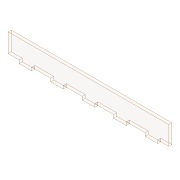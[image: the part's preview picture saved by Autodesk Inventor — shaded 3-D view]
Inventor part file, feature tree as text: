
AUTODESK INVENTOR PART (.ipt)
format: ipt  version: 2020 (Build 240168000, 168)  size: 113,152 bytes
history: native  units: in
note: dims shown in document units (in); Inventor stores cm internally (conversion verified against a paired STEP export)
features: extrude x2, sketch x2
ambient origin geometry x8: Origin, YZ Plane, XZ Plane, XY Plane, X Axis, Y Axis, Z Axis, Center Point
bodies: Solid1 (feature_tree)
feature tree (4):
  extrude  "Extrusion1"  Depth=1.1811in
  extrude  "Extrusion2"  Depth=0.7874in
  sketch  "Sketch1"  dims[d0=10.0394in d1=1.1811in]
  sketch  "Sketch2"  dims[d2=0.1969in d3=0.0in d4=0.7874in d5=0.1969in d6=0.689in d7=1.9685in d9=1.9685in d10=0.3937in d12=0.3937in d14=0.689in d15=0.1969in d16=0.0in]
